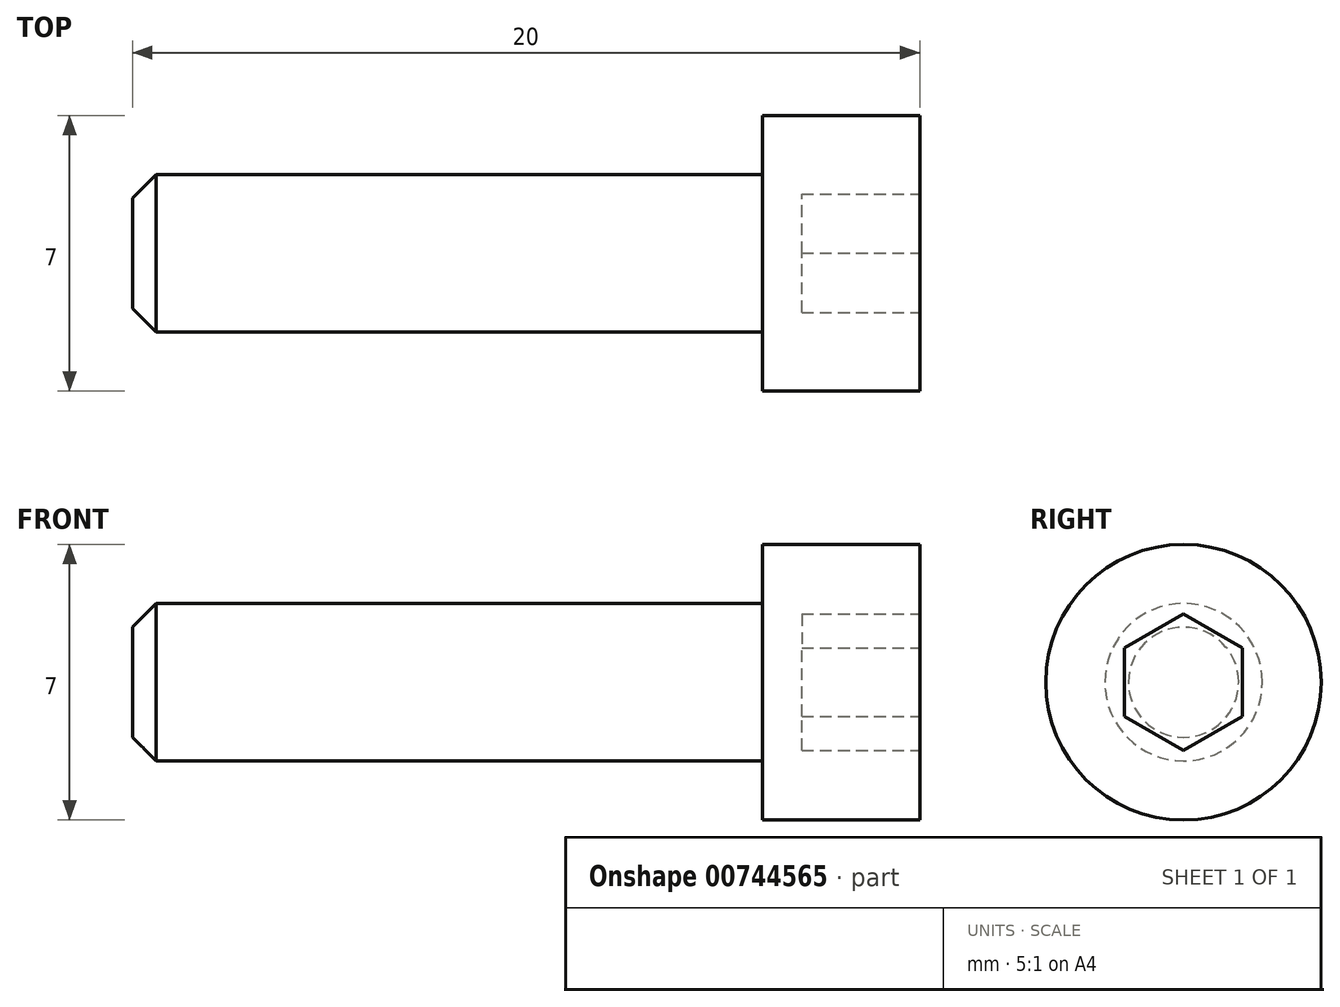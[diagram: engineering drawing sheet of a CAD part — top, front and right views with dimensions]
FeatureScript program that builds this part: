
annotation { "Feature Type Name" : "Feature", "Feature Type Description" : "" }
export const myFeature = defineFeature(function(context is Context, id is Id, definition is map)
    precondition{}
    {
        {
            var Q0;
            Q0=qCreatedBy(makeId("Right.planeOp"),FACE);
            var sketch = newSketch(context, id + "F0", { "sketchPlane" : qUnion([Q0])});
            skCircle(sketch, "E0", {"center": v(0, 0) * mm, "radius": 2 * mm});
            skSolve(sketch);
        }
        {
            var Q0;
            Q0=qSketchRegion(id+"F0",true);
            extrude(context, id + "F1", {"entities" : qUnion([Q0]), "oppositeDirection" : true, "depth" : 16 * mm, "offsetDistance" : 25 * mm});
        }
        {
            var Q0;
            Q0=makeQuery(id+"F1.opExtrude","CAP_FACE",FACE,{"disambiguationData":[OSD([sQuery(id+"F0.wireOp",EDGE,"E0")])],"isStart":true});
            var sketch = newSketch(context, id + "F2", { "sketchPlane" : qUnion([Q0])});
            skCircle(sketch, "E1", {"center": v(0, 0) * mm, "radius": 3.5 * mm});
            skSolve(sketch);
        }
        {
            var Q0;
            Q0 = qSketchRegion(id + "F2", true);
            extrude(context, id + "F3", {"entities" : qUnion([Q0]), "operationType" : NewBodyOperationType.ADD, "depth" : 4 * mm, "offsetDistance" : 25 * mm});
        }
        {
            var Q0;
            Q0=makeQuery(id+"F3.opExtrude","CAP_FACE",FACE,{"disambiguationData":[OSD([sQuery(id+"F2.wireOp",EDGE,"E1")])],"isStart":false});
            var sketch = newSketch(context, id + "F4", { "sketchPlane" : qUnion([Q0])});
            skCircle(sketch, "E2.cCircle", {"center": v(0, 0) * mm, "radius": 1.5 * mm, "construction": true});
            skLineSegment(sketch, "E2.0", {"start": v(0, 1.73) * mm, "end": v(1.5, 0.87) * mm});
            skLineSegment(sketch, "E2.1", {"start": v(1.5, 0.87) * mm, "end": v(1.5, -0.87) * mm});
            skLineSegment(sketch, "E2.2", {"start": v(1.5, -0.87) * mm, "end": v(0, -1.73) * mm});
            skLineSegment(sketch, "E2.3", {"start": v(0, -1.73) * mm, "end": v(-1.5, -0.87) * mm});
            skLineSegment(sketch, "E2.4", {"start": v(-1.5, -0.87) * mm, "end": v(-1.5, 0.87) * mm});
            skLineSegment(sketch, "E2.5", {"start": v(-1.5, 0.87) * mm, "end": v(0, 1.73) * mm});
            skPoint(sketch, "E2.0.midPoint", {"position": v(0.75, 1.3) * mm});
            skSolve(sketch);
        }
        {
            var Q0;
            Q0 = qSketchRegion(id + "F4", true);
            extrude(context, id + "F5", {"entities" : qUnion([Q0]), "operationType" : NewBodyOperationType.REMOVE, "oppositeDirection" : true, "depth" : 3 * mm, "offsetDistance" : 25 * mm});
        }
        {
            var Q0;
            Q0=makeQuery(id+"F1.opExtrude","CAP_FACE",FACE,{"disambiguationData":[OSD([sQuery(id+"F0.wireOp",EDGE,"E0")])],"isStart":false});
            chamfer(context, id + "F6", {"entities" : qUnion([Q0]), "width" : 0.6 * mm, "tangentPropagation" : true});
        }
    });
